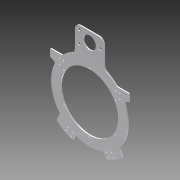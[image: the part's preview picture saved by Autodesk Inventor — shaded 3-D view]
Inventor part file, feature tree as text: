
AUTODESK INVENTOR PART (.ipt)
format: ipt  version: 2014 SP1 (Build 180222100, 222)  size: 468,992 bytes
history: native  units: in
note: dims shown in document units (in); Inventor stores cm internally (conversion verified against a paired STEP export)
features: reference x20, sketch x8, extrude x7, fillet x3, projected_geometry x1
ambient origin geometry x8: Origin, YZ Plane, XZ Plane, XY Plane, X Axis, Y Axis, Z Axis, Center Point
bodies: Solid1 (feature_tree)
feature tree (39):
  extrude  "Extrusion1"  Depth=10.43in
  sketch  "Sketch2"  dims[d2=10.83in d3=0.266in]
  extrude  "Extrusion5"  Depth=0.266in
  extrude  "Extrusion4"  Depth=0.125in TaperAngle=0.0deg
  fillet  "Fillet1"  Radius=0.25in
  fillet  "Fillet2"  Radius=0.375in
  fillet  "Fillet3"  Radius=0.375in
  extrude  "Extrusion6"  Depth=0.25in TaperAngle=0.0deg
  extrude  "Extrusion10"  Depth=0.125in
  extrude  "Extrusion11"  Depth=0.25in
  sketch  "Sketch8"  dims[d27=0.25in d28=0.125in d29=0.0in]
  extrude  "Extrusion12"  Depth=0.125in TaperAngle=0.0deg
  sketch  "Sketch1"  dims[d0=14.0in d1=10.43in]
  reference  "Reference1"
  reference  "Reference2"
  reference  "Reference3"
  reference  "Reference4"
  reference  "Reference5"
  reference  "Reference6"
  reference  "Reference7"
  reference  "Reference9"
  projected_geometry  "Projected Loop1"
  sketch  "Sketch3"  dims[d4=2.3622in d6=360.0deg d8=0.125in d9=0.0in d11=0.25in d12=0.375in d13=0.375in]
  reference  "Reference10"
  reference  "Reference11"
  sketch  "Sketch4"  dims[d14=0.25in d21=5.0in d22=0.0in]
  reference  "Reference12"
  reference  "Reference13"
  sketch  "Sketch6"  dims[d23=0.125in d24=0.2in]
  reference  "Reference14"
  reference  "Reference15"
  reference  "Reference16"
  reference  "Reference17"
  reference  "Reference18"
  reference  "Reference19"
  sketch  "Sketch7"  dims[d25=0.2in d26=0.25in]
  sketch  "Sketch9"  dims[d30=0.125in d31=0.125in d32=0.125in d33=1.0in d34=0.0in d37=1.05in d50=1.0in d51=1.0in d52=0.75in d53=0.75in d54=0.75in d55=1.0in d56=0.49in d57=0.49in d58=0.49in d63=2.3in d64=0.125in d65=0.0in d66=0.0625in d67=0.0in d68=12.25in d69=1.25in d70=11.5in d71=1.5in d72=1.5in d74=1.5in d75=2.25in d76=1.5in d77=1.5in d78=1.25in d79=1.25in d80=1.45in d81=7.25in d82=1.45in d83=1.0in d84=0.0in]
  reference  "Reference20"
  reference  "Reference21"
